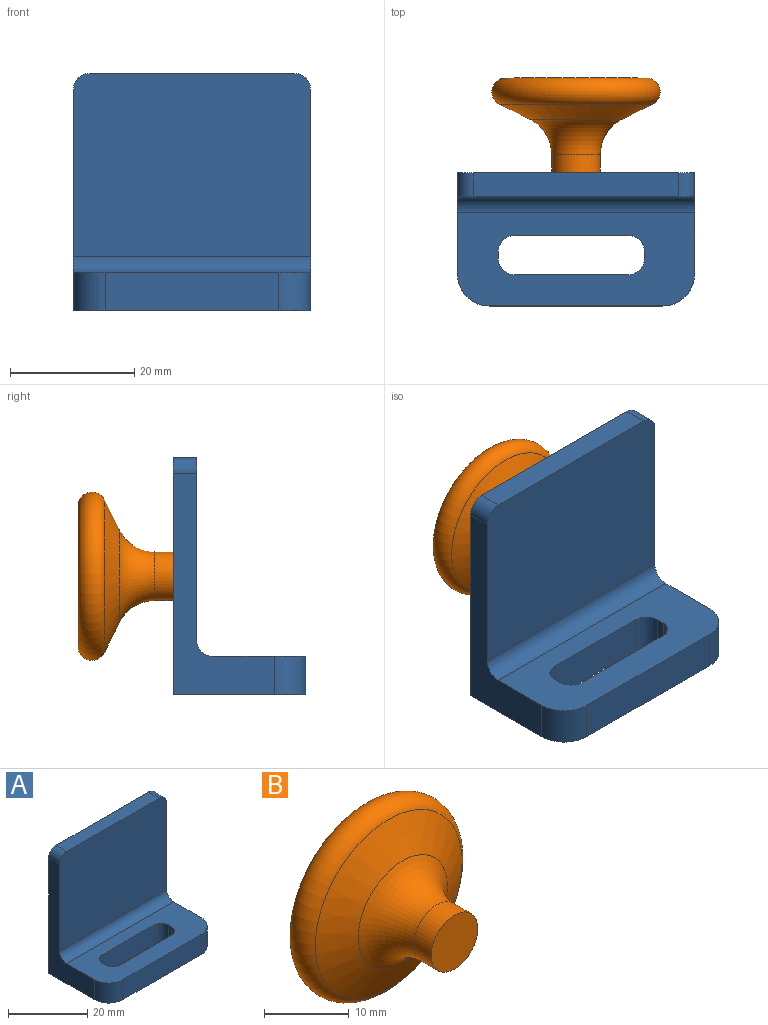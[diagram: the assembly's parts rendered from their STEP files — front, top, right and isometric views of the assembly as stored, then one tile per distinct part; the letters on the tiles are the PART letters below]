
ASSEMBLY  parts=2 mates=1
PART A: 21 faces, bbox 38.1x21.3x38.1 mm
  f0: plane 38.1x29.42mm, normal (0,-1,0), area 1117.9mm2, adj f1,f2,f4,f6,f7,f10
  f1: plane 33.02x3.81mm, normal (0,0,1), area 125.8mm2, adj f0,f5,f6,f7
  f2: plane 35.56x16.26mm, normal (-1,0,0), area 213.4mm2, adj f0,f3,f5,f6,f8,f10,f19
  f3: plane 38.1x21.34mm, normal (0,0,-1), area 659.6mm2, adj f2,f4,f5,f9,f11,f12,f13,f14
  f4: plane 35.56x16.26mm, normal (1,0,0), area 213.4mm2, adj f0,f3,f5,f7,f8,f10,f20
  f5: plane 38.1x38.1mm, normal (0,1,0), area 1448.8mm2, adj f1,f2,f3,f4,f6,f7
  f6: cylinder r=2.54mm len=3.81mm, axis (0,-1,0), area 15.2mm2, adj f0,f1,f2,f5
  f7: cylinder r=2.54mm len=3.81mm, axis (0,1,0), area 15.2mm2, adj f0,f1,f4,f5
  f8: plane 38.1x14.99mm, normal (0,0,1), area 417.7mm2, adj f2,f4,f9,f10,f11,f12,f13,f14
  f9: plane 27.94x6.15mm, normal (0,-1,0), area 171.7mm2, adj f3,f8,f19,f20
  f10: cylinder r=2.54mm len=38.1mm, axis (-1,0,0), area 152mm2, adj f0,f2,f4,f8
  f11: plane 6.15x1.21mm, normal (-1,0,0), area 7.5mm2, adj f3,f8,f12,f18
  f12: cylinder r=2.54mm len=6.15mm, axis (0,0,1), area 24.5mm2, adj f3,f8,f11,f13
  f13: plane 18.39x6.15mm, normal (0,-1,0), area 113mm2, adj f3,f8,f12,f14
  f14: cylinder r=2.54mm len=6.15mm, axis (0,0,1), area 24.5mm2, adj f3,f8,f13,f15
  f15: plane 6.15x1.21mm, normal (1,0,0), area 7.5mm2, adj f3,f8,f14,f16
  f16: cylinder r=2.54mm len=6.15mm, axis (0,0,1), area 24.5mm2, adj f3,f8,f15,f17
  f17: plane 18.39x6.15mm, normal (0,1,0), area 113mm2, adj f3,f8,f16,f18
  f18: cylinder r=2.54mm len=6.15mm, axis (0,0,1), area 24.5mm2, adj f3,f8,f11,f17
  f19: cylinder r=5.08mm len=6.15mm, axis (0,0,1), area 49mm2, adj f2,f3,f8,f9
  f20: cylinder r=5.08mm len=6.15mm, axis (0,0,-1), area 49mm2, adj f3,f4,f8,f9
PART B: 6 faces, bbox 29.3x15.3x29.3 mm
  f0: plane 7.81x7.81mm, normal (0,-1,0), area 47.9mm2, adj f5
  f1: cone r=0mm half-angle=66.9deg, axis (0,1,0), area 457.7mm2, adj f2
  f2: torus R=11.27mm, axis (0,-1,0), area 465.8mm2, adj f1,f3
  f3: cone r=7.45mm half-angle=63.8deg, axis (0,1,0), area 331.9mm2, adj f2,f4
  f4: torus R=10.25mm, axis (0,-1,0), area 228.3mm2, adj f3,f5
  f5: cylinder r=3.9mm len=7.81mm, axis (0,-1,0), area 72.7mm2, adj f0,f4
PLACE A t=(4.07,10.92,18.57)mm
PLACE B t=(4.82,10.92,18.95)mm
MATE fastened A.f5 <-> B.f1  axis (0,1,0) through (4.82,10.92,18.95)mm
